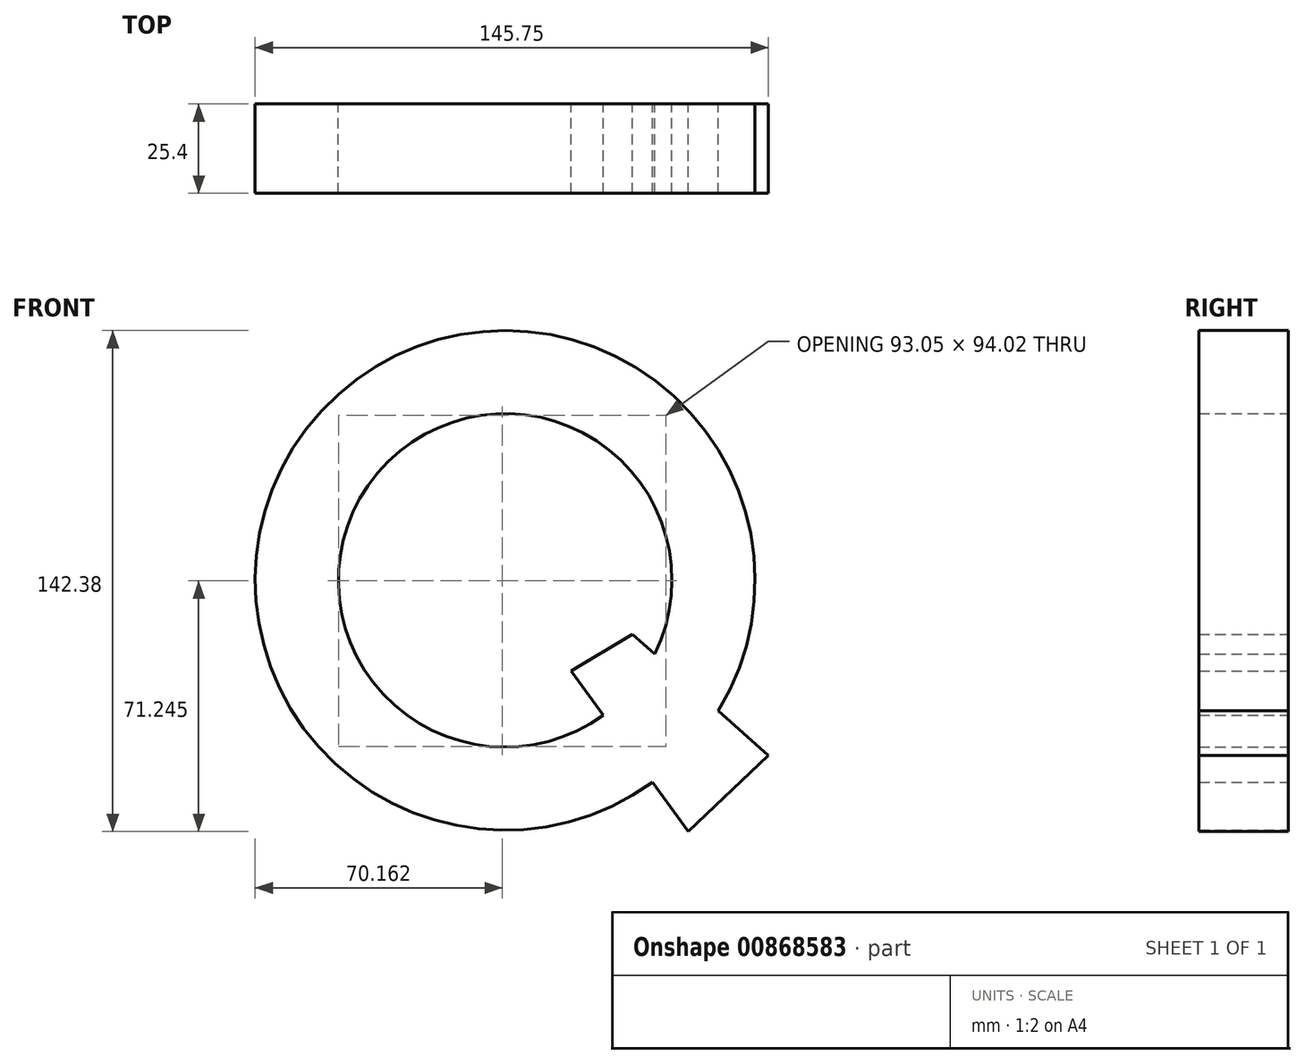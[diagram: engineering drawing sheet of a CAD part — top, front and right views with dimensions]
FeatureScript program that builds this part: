
annotation { "Feature Type Name" : "Feature", "Feature Type Description" : "" }
export const myFeature = defineFeature(function(context is Context, id is Id, definition is map)
    precondition{}
    {
        {
            var Q0;
            Q0=qCreatedBy(makeId("Front.planeOp"),FACE);
            var sketch = newSketch(context, id + "F0", { "sketchPlane" : qUnion([Q0])});
            skArc(sketch, "E0", {"start": v(60.55, -37.05) * mm, "mid": v(-52.18, 48.13) * mm, "end": v(41.8, -57.37) * mm});
            skArc(sketch, "E1", {"start": v(42.47, -20.97) * mm, "mid": v(-36.24, 30.5) * mm, "end": v(27.91, -38.27) * mm});
            skLineSegment(sketch, "E2", {"start": v(18.76, -25.7) * mm, "end": v(27.91, -38.27) * mm});
            skLineSegment(sketch, "E3", {"start": v(52, -71.39) * mm, "end": v(74.76, -49.7) * mm});
            skLineSegment(sketch, "E4", {"start": v(74.76, -49.7) * mm, "end": v(60.55, -37.05) * mm});
            skLineSegment(sketch, "E5", {"start": v(36.18, -15.38) * mm, "end": v(18.76, -25.7) * mm});
            skLineSegment(sketch, "E6.trimOffspring", {"start": v(42.47, -20.97) * mm, "end": v(36.18, -15.38) * mm});
            skLineSegment(sketch, "E7.trimOffspring", {"start": v(41.8, -57.37) * mm, "end": v(52, -71.39) * mm});
            skSolve(sketch);
        }
        {
            var Q0;
            Q0=makeQuery(id+"F0.imprint","IMPRINT",FACE,{"disambiguationData":[TD([[makeQuery(id+"F0.imprint","IMPRINT",EDGE,{"derivedFrom":sQuery(id+"F0.wireOp",EDGE,"E0")}),1.0]])]});
            extrude(context, id + "F1", {"entities" : qUnion([Q0]), "depth" : 25.4 * mm, "offsetDistance" : 25.4 * mm});
        }
    });
